FCSTD DOCUMENT  (FreeCAD 0.21R33668 +26 (Git))
Label: Rotation-000
License: All rights reserved
LicenseURL: http://en.wikipedia.org/wiki/All_rights_reserved
objects: App::DocumentObjectGroup×3, Sketcher::SketchObject×1, PartDesign::Body×1, App::FeaturePython×1, PartDesign::CoordinateSystem×1, App::Link×1, App::Part×1
note: 3 computed .brp shape members not serialized (recipe doc carries the construction recipe); baked Part::Feature solids carry a one-line shape summary decoded from their .brp

FEATURE [Sketcher::SketchObject] Sketch
  FullyConstrained = true
  MapMode = 5
  Placement = pos=(0,0,0) rot=(0.57735,0.57735,0.57735;2.0944rad)
  Support = -> [YZ_Plane]
  expr: Constraints[3] = Variables.rotation
  sketch-geometry (1):
    g0: LineSegment StartX=0 StartY=20 StartZ=0 EndX=-29.7764 EndY=23.6561 EndZ=0
  constraints (4):
    c: PointOnObject(g0,g-2)
    c: DistanceY(g-1,g0) = 20
    c: Distance(g0) = 30
    c: Angle(g-1,g0) = 3.01942
FEATURE [PartDesign::Body] Body  label="Corps"
  Group = -> [Sketch]
  Origin = -> Origin
FEATURE [App::FeaturePython] Variables  # WARN: FeaturePython — macro-defined, semantics opaque (R4)
  Type = App::PropertyContainer
  rotation = 173
FEATURE [App::DocumentObjectGroup] Parts
  Group = -> [Body]
FEATURE [PartDesign::CoordinateSystem] LCS_Origin
  AttacherType = Attacher::AttachEngine3D
  MapMode = 2
  Support = -> [X_Axis002]
FEATURE [App::DocumentObjectGroup] Constraints
FEATURE [App::DocumentObjectGroup] Configurations
FEATURE [App::Link] Corps  label="Corps001"
  LinkedObject = -> Body
FEATURE [App::Part] Assembly
  AssemblyType = Part::Link
  Group = -> [LCS_Origin,Constraints,Variables,Configurations,Corps]
  Origin = -> Origin002
  Type = Assembly
